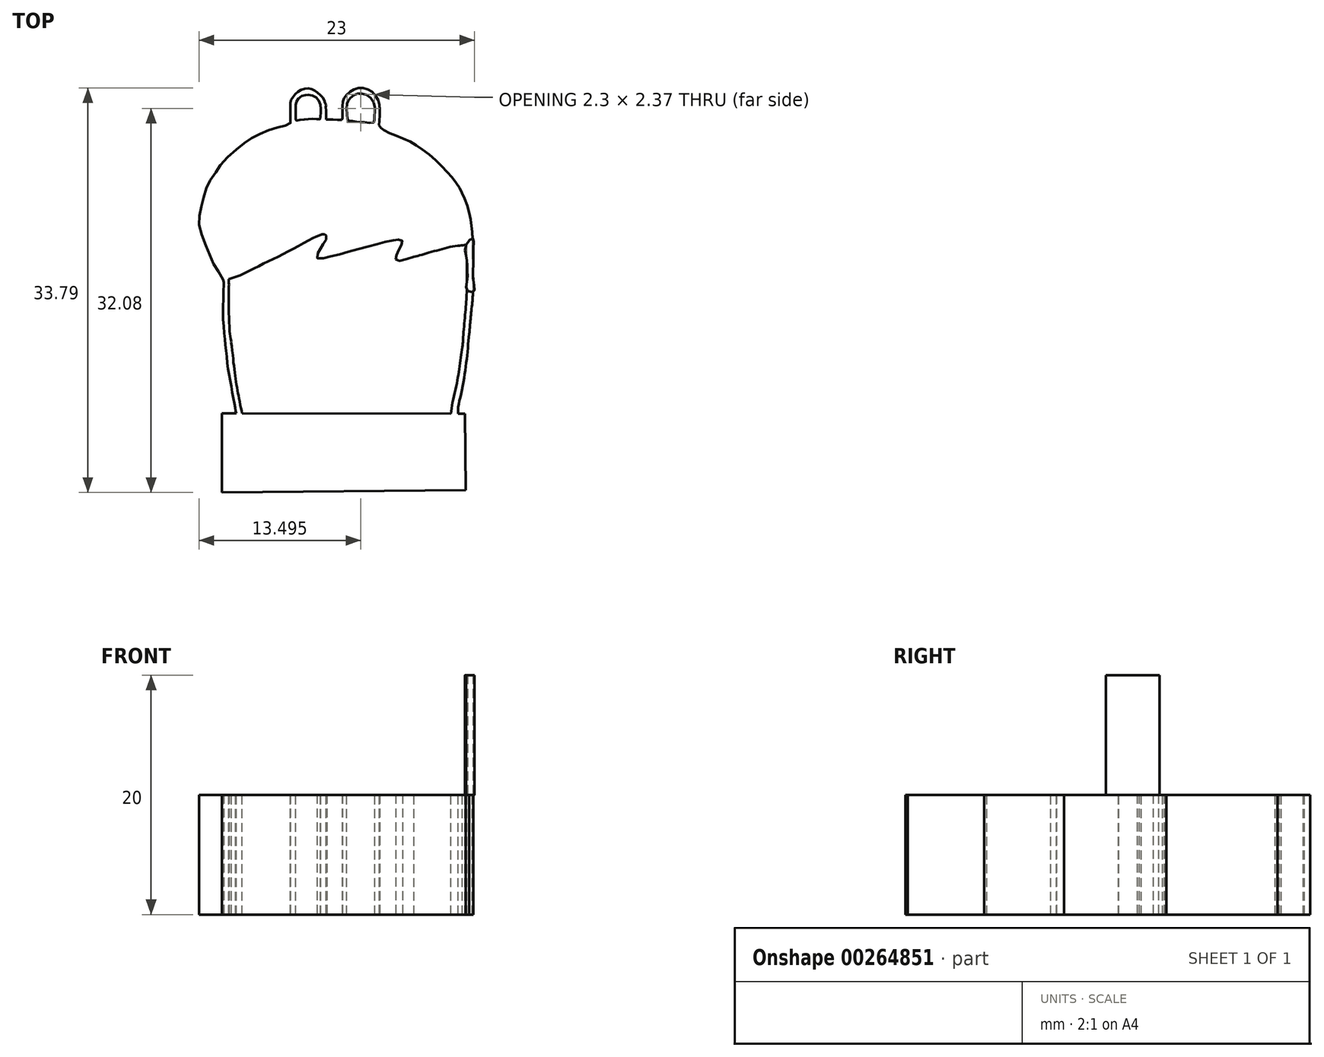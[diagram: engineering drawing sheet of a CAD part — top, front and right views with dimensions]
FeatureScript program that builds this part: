
annotation { "Feature Type Name" : "Feature", "Feature Type Description" : "" }
export const myFeature = defineFeature(function(context is Context, id is Id, definition is map)
    precondition{}
    {
        {
            var Q0;
            Q0=qCreatedBy(makeId("Top.planeOp"),FACE);
            var sketch = newSketch(context, id + "F0", { "sketchPlane" : qUnion([Q0])});
            skFitSpline(sketch, "E0", {"points": [v(-8.8, 2.1) * mm, v(-8.4, 2.24) * mm, v(-7.67, 2.52) * mm, v(-6.78, 2.96) * mm, v(-5.81, 3.45) * mm, v(-4.83, 3.93) * mm, v(-3.79, 4.44) * mm, v(-2.68, 5.05) * mm, v(-1.76, 5.56) * mm, v(-1.35, 5.71) * mm, v(-1.03, 5.86) * mm, v(-0.82, 5.85) * mm, v(-0.68, 5.76) * mm], "startDerivative": vector(5.65, 1.9) * mm, "endDerivative": vector(3.17, -2.45) * mm});
            skFitSpline(sketch, "E1", {"points": [v(-0.68, 5.76) * mm, v(-0.61, 5.57) * mm, v(-0.78, 5.3) * mm, v(-0.97, 5) * mm, v(-1.11, 4.72) * mm, v(-1.3, 4.4) * mm, v(-1.42, 4.12) * mm, v(-1.41, 3.83) * mm, v(-1.02, 3.82) * mm, v(-0.43, 3.99) * mm, v(0.48, 4.17) * mm, v(1.43, 4.47) * mm, v(2.69, 4.8) * mm, v(3.65, 5.05) * mm, v(4.39, 5.26) * mm, v(5.07, 5.36) * mm, v(5.34, 5.41) * mm, v(5.58, 5.38) * mm, v(5.7, 5.27) * mm, v(5.62, 5.03) * mm, v(5.5, 4.75) * mm, v(5.3, 4.37) * mm, v(5.18, 4.08) * mm, v(5.12, 3.85) * mm, v(5.18, 3.65) * mm, v(5.42, 3.64) * mm, v(6.02, 3.76) * mm, v(6.65, 3.96) * mm], "startDerivative": vector(4.5, -7.51) * mm, "endDerivative": vector(13.56, 4.53) * mm});
            skFitSpline(sketch, "E2", {"points": [v(6.65, 3.96) * mm, v(7.15, 4.1) * mm, v(7.84, 4.32) * mm, v(8.74, 4.54) * mm, v(9.73, 4.81) * mm, v(10.44, 4.9) * mm, v(10.8, 4.95) * mm, v(11, 4.95) * mm, v(11.03, 4.8) * mm, v(11.04, 4) * mm, v(11.05, 3.1) * mm, v(11.06, 2.1) * mm, v(11.05, 1.1) * mm, v(10.99, 0) * mm, v(10.86, -1.43) * mm, v(10.74, -2.88) * mm, v(10.69, -3.57) * mm], "startDerivative": vector(9.32, 2.38) * mm, "endDerivative": vector(-1.16, -10.46) * mm});
            skFitSpline(sketch, "E3", {"points": [v(11.26, -2.47) * mm, v(11.32, -1.74) * mm, v(11.43, -0.57) * mm, v(11.54, 0.6) * mm, v(11.58, 1.5) * mm, v(11.56, 2.8) * mm, v(11.55, 3.79) * mm, v(11.52, 4.76) * mm, v(11.52, 5.42) * mm, v(11.49, 6.07) * mm], "startDerivative": vector(0.56, 7) * mm, "endDerivative": vector(-0.91, 7.3) * mm});
            skFitSpline(sketch, "E4", {"points": [v(11.49, 6.07) * mm, v(11.41, 6.74) * mm, v(11.26, 7.62) * mm, v(10.96, 8.63) * mm, v(10.63, 9.37) * mm, v(10.37, 9.84) * mm, v(9.84, 10.58) * mm, v(9.17, 11.33) * mm, v(8.18, 12.3) * mm, v(7.1, 13.1) * mm, v(6.27, 13.6) * mm, v(5.2, 14.08) * mm, v(4.42, 14.38) * mm, v(3.93, 14.71) * mm, v(3.83, 14.79) * mm, v(3.73, 14.97) * mm, v(3.75, 15.34) * mm], "startDerivative": vector(-1.2, 10.67) * mm, "endDerivative": vector(-0.34, 9.32) * mm});
            skFitSpline(sketch, "E5", {"points": [v(3.75, 15.34) * mm, v(3.78, 16.03) * mm, v(3.75, 16.66) * mm, v(3.63, 17.11) * mm, v(3.24, 17.64) * mm, v(2.83, 17.94) * mm, v(2.27, 18.07) * mm, v(1.8, 18.01) * mm, v(1.35, 17.8) * mm, v(1, 17.5) * mm, v(0.78, 17.16) * mm, v(0.7, 16.86) * mm, v(0.66, 16.36) * mm, v(0.66, 16.03) * mm, v(0.66, 15.73) * mm, v(0.65, 15.47) * mm, v(0.62, 15.42) * mm, v(0.33, 15.41) * mm, v(-0.19, 15.43) * mm, v(-0.5, 15.43) * mm, v(-0.7, 15.43) * mm], "startDerivative": vector(0.4, 10.64) * mm, "endDerivative": vector(-5.55, -0.03) * mm});
            skCircle(sketch, "E6", {"center": v(6.09, -0.5) * mm, "radius": 3.15 * mm});
            skPoint(sketch, "E6.first.point", {"position": v(5.98, 2.65) * mm});
            skPoint(sketch, "E6.second.point", {"position": v(6.02, -3.65) * mm});
            skPoint(sketch, "E6.third.point", {"position": v(9.22, -0.2) * mm});
            skCircle(sketch, "E7", {"center": v(6.08, -0.54) * mm, "radius": 2.63 * mm});
            skPoint(sketch, "E7.first.point", {"position": v(5.98, 2.1) * mm});
            skPoint(sketch, "E7.second.point", {"position": v(5.98, -3.17) * mm});
            skPoint(sketch, "E7.third.point", {"position": v(8.7, -0.58) * mm});
            skCircle(sketch, "E8", {"center": v(7.16, -0.53) * mm, "radius": 1.28 * mm});
            skPoint(sketch, "E8.first.point", {"position": v(7.12, 0.75) * mm});
            skPoint(sketch, "E8.second.point", {"position": v(7.22, -1.8) * mm});
            skPoint(sketch, "E8.third.point", {"position": v(8.43, -0.49) * mm});
            skCircle(sketch, "E9", {"center": v(-4.02, -0.63) * mm, "radius": 3.11 * mm});
            skPoint(sketch, "E9.first.point", {"position": v(-4.2, 2.47) * mm});
            skPoint(sketch, "E9.second.point", {"position": v(-3.86, -3.74) * mm});
            skPoint(sketch, "E9.third.point", {"position": v(-1.05, 0.3) * mm});
            skCircle(sketch, "E10", {"center": v(-4.04, -0.66) * mm, "radius": 2.65 * mm});
            skPoint(sketch, "E10.first.point", {"position": v(-4.2, 1.99) * mm});
            skPoint(sketch, "E10.second.point", {"position": v(-3.9, -3.3) * mm});
            skPoint(sketch, "E10.third.point", {"position": v(-1.39, -0.71) * mm});
            skCircle(sketch, "E11", {"center": v(-2.97, -0.61) * mm, "radius": 1.26 * mm});
            skPoint(sketch, "E11.first.point", {"position": v(-2.97, 0.64) * mm});
            skPoint(sketch, "E11.second.point", {"position": v(-2.96, -1.87) * mm});
            skPoint(sketch, "E11.third.point", {"position": v(-1.72, -0.58) * mm});
            skFitSpline(sketch, "E12", {"points": [v(0.31, -3.75) * mm, v(0.56, -3.78) * mm, v(0.87, -3.93) * mm, v(0.95, -3.99) * mm, v(1.05, -3.93) * mm, v(1.33, -3.75) * mm, v(1.71, -3.7) * mm, v(2, -3.87) * mm, v(2.13, -4.19) * mm, v(2.02, -4.46) * mm, v(1.77, -4.62) * mm, v(1.4, -4.73) * mm, v(1, -4.78) * mm, v(0.6, -4.75) * mm, v(0.25, -4.68) * mm, v(0, -4.54) * mm, v(-0.17, -4.24) * mm, v(-0.13, -3.95) * mm, v(0.05, -3.79) * mm, v(0.31, -3.75) * mm]});
            skFitSpline(sketch, "E13", {"points": [v(-3.23, 15.5) * mm, v(-3.24, 16.06) * mm, v(-3.24, 16.53) * mm, v(-3.2, 16.85) * mm, v(-3.06, 17.13) * mm, v(-2.75, 17.38) * mm, v(-2.45, 17.48) * mm, v(-2.2, 17.5) * mm, v(-1.77, 17.42) * mm, v(-1.43, 17.19) * mm, v(-1.2, 16.82) * mm, v(-1.16, 16.43) * mm, v(-1.15, 16.01) * mm, v(-1.16, 15.67) * mm, v(-1.18, 15.48) * mm, v(-1.42, 15.47) * mm, v(-1.84, 15.49) * mm, v(-2.2, 15.48) * mm, v(-2.65, 15.42) * mm, v(-3.07, 15.37) * mm, v(-3.22, 15.35) * mm, v(-3.23, 15.5) * mm]});
            skFitSpline(sketch, "E14", {"points": [v(1.07, 15.46) * mm, v(1.04, 15.89) * mm, v(1.04, 16.39) * mm, v(1.06, 16.83) * mm, v(1.12, 16.97) * mm, v(1.2, 17.1) * mm, v(1.43, 17.33) * mm, v(1.7, 17.5) * mm, v(1.96, 17.59) * mm, v(2.28, 17.6) * mm, v(2.68, 17.5) * mm, v(3.04, 17.22) * mm, v(3.3, 16.78) * mm, v(3.37, 16.4) * mm, v(3.36, 16.07) * mm, v(3.35, 15.74) * mm, v(3.34, 15.45) * mm, v(3.32, 15.22) * mm, v(3.26, 15.18) * mm, v(3, 15.16) * mm, v(2.56, 15.2) * mm, v(2.2, 15.23) * mm, v(1.9, 15.25) * mm, v(1.63, 15.28) * mm, v(1.37, 15.31) * mm, v(1.16, 15.33) * mm, v(1.1, 15.37) * mm, v(1.07, 15.46) * mm]});
            skLineSegment(sketch, "E15", {"start": v(-9.39, -9.12) * mm, "end": v(-9.39, -15.72) * mm});
            skLineSegment(sketch, "E16", {"start": v(-9.39, -15.72) * mm, "end": v(10.95, -15.53) * mm});
            skLineSegment(sketch, "E17", {"start": v(10.95, -15.53) * mm, "end": v(10.89, -9.14) * mm});
            skFitSpline(sketch, "E18", {"points": [v(-0.7, 15.43) * mm, v(-0.7, 16.1) * mm, v(-0.7, 16.56) * mm, v(-0.7, 16.65) * mm, v(-0.77, 16.82) * mm, v(-0.88, 17.1) * mm, v(-1.04, 17.33) * mm, v(-1.35, 17.64) * mm, v(-1.71, 17.88) * mm, v(-2.07, 18.03) * mm, v(-2.5, 18) * mm, v(-2.92, 17.83) * mm, v(-3.26, 17.56) * mm, v(-3.54, 17.2) * mm, v(-3.67, 16.9) * mm, v(-3.7, 16.38) * mm, v(-3.69, 16.04) * mm, v(-3.68, 15.66) * mm], "startDerivative": vector(0.03, 8.48) * mm, "endDerivative": vector(0.2, -6.68) * mm});
            skFitSpline(sketch, "E19", {"points": [v(-3.68, 15.66) * mm, v(-3.68, 15.28) * mm, v(-3.68, 15.13) * mm, v(-3.68, 15.1) * mm, v(-3.9, 15) * mm, v(-4.43, 14.84) * mm, v(-4.92, 14.72) * mm, v(-5.58, 14.51) * mm, v(-6.18, 14.25) * mm, v(-6.79, 13.95) * mm, v(-7.26, 13.68) * mm, v(-7.78, 13.27) * mm, v(-8.45, 12.7) * mm, v(-9.15, 12.05) * mm, v(-9.63, 11.47) * mm, v(-9.92, 11) * mm, v(-10.32, 10.44) * mm, v(-10.61, 9.87) * mm, v(-10.8, 9.34) * mm, v(-10.97, 8.67) * mm, v(-11.15, 8.03) * mm, v(-11.26, 7.36) * mm, v(-11.3, 6.75) * mm, v(-11.15, 6.09) * mm, v(-10.84, 5.13) * mm, v(-10.51, 4.42) * mm, v(-10.25, 3.68) * mm, v(-9.95, 3.17) * mm, v(-9.6, 2.63) * mm, v(-9.29, 2.08) * mm], "startDerivative": vector(0.15, -14.8) * mm, "endDerivative": vector(7.87, -15.58) * mm});
            skFitSpline(sketch, "E20", {"points": [v(-9.29, 2.08) * mm, v(-9.24, 1.84) * mm, v(-9.24, 1.67) * mm, v(-9.29, 0.19) * mm, v(-9.29, -1.17) * mm, v(-9.18, -2.54) * mm, v(-9.08, -3.52) * mm, v(-8.96, -4.65) * mm, v(-8.83, -5.7) * mm, v(-8.63, -6.74) * mm, v(-8.44, -7.8) * mm, v(-8.3, -8.55) * mm, v(-8.25, -8.93) * mm], "startDerivative": vector(1.42, -6.07) * mm, "endDerivative": vector(0.55, -6.27) * mm});
            skPoint(sketch, "E21", {"position": v(-7.7, -9.12) * mm});
            skPoint(sketch, "E22", {"position": v(-8.2, -9.12) * mm});
            skFitSpline(sketch, "E23", {"points": [v(-8.25, -8.93) * mm, v(-8.2, -9.12) * mm], "startDerivative": vector(0.05, -0.2) * mm, "endDerivative": vector(0.05, -0.2) * mm});
            skFitSpline(sketch, "E24", {"points": [v(-7.7, -9.12) * mm, v(-7.84, -8.5) * mm, v(-7.99, -7.74) * mm, v(-8.08, -7.23) * mm, v(-8.21, -6.57) * mm, v(-8.3, -5.92) * mm, v(-8.4, -5.08) * mm, v(-8.51, -4.03) * mm, v(-8.62, -3.09) * mm, v(-8.6, -3.09) * mm], "startDerivative": vector(-1.1, 5.28) * mm, "endDerivative": vector(0.63, -0.3) * mm});
            skFitSpline(sketch, "E25", {"points": [v(-8.6, -3.09) * mm, v(-8.72, -2.5) * mm, v(-8.77, -1.86) * mm, v(-8.8, -1) * mm, v(-8.81, 0) * mm, v(-8.83, 1.11) * mm, v(-8.8, 1.47) * mm, v(-8.8, 1.75) * mm, v(-8.8, 2.1) * mm], "startDerivative": vector(-1.04, 4.82) * mm, "endDerivative": vector(0.02, 3.77) * mm});
            skLineSegment(sketch, "E26", {"start": v(-8.2, -9.12) * mm, "end": v(-9.39, -9.12) * mm});
            skLineSegment(sketch, "E27", {"start": v(-7.7, -9.12) * mm, "end": v(9.72, -9.14) * mm});
            skLineSegment(sketch, "E28", {"start": v(10.89, -9.14) * mm, "end": v(10.34, -9.14) * mm});
            skFitSpline(sketch, "E29", {"points": [v(10.69, -3.57) * mm, v(10.53, -4.5) * mm, v(10.39, -5.58) * mm, v(10.2, -6.68) * mm, v(9.88, -8.08) * mm, v(9.72, -9.14) * mm], "startDerivative": vector(-0.8, -4.96) * mm, "endDerivative": vector(-0.61, -5.17) * mm});
            skFitSpline(sketch, "E30", {"points": [v(11.26, -2.47) * mm, v(11.15, -3.45) * mm, v(11.04, -4.57) * mm, v(10.9, -5.72) * mm, v(10.69, -7) * mm, v(10.42, -8.1) * mm, v(10.32, -8.78) * mm, v(10.34, -9.14) * mm], "startDerivative": vector(-0.71, -6.55) * mm, "endDerivative": vector(0.44, -3.74) * mm});
            skLineSegment(sketch, "E31", {"start": v(10.34, -9.14) * mm, "end": v(9.72, -9.14) * mm});
            skSolve(sketch);
        }
        {
            var Q0;
            Q0=makeQuery(id+"F0.imprint","IMPRINT",FACE,{"disambiguationData":[TD([[makeQuery(id+"F0.imprint","IMPRINT",EDGE,{"derivedFrom":sQuery(id+"F0.wireOp",EDGE,"E0")}),1.0]])]});
            extrude(context, id + "F1", {"entities" : qUnion([Q0]), "oppositeDirection" : true, "depth" : 10 * mm});
        }
        {
            var Q0;
            Q0=qCreatedBy(makeId("Top.planeOp"),FACE);
            cPlane(context, id + "F2", {"entities" : qUnion([Q0]), "cplaneType" : CPlaneType.OFFSET, "offset" : 0 * mm, "width" : 150 * mm, "height" : 150 * mm});
        }
        {
            var Q0;
            Q0=qCreatedBy(id+"F2.planeOp",FACE);
            var sketch = newSketch(context, id + "F3", { "sketchPlane" : qUnion([Q0])});
            skFitSpline(sketch, "E32", {"points": [v(10.98, 4.97) * mm, v(11, 3.98) * mm, v(11.08, 3.09) * mm, v(11.08, 2.02) * mm, v(11.04, 1.2) * mm, v(11.63, 1.06) * mm, v(11.63, 1.71) * mm, v(11.56, 2.67) * mm, v(11.6, 3.5) * mm, v(11.6, 4.7) * mm, v(11.56, 5.49) * mm, v(10.98, 4.97) * mm]});
            skSolve(sketch);
        }
        {
            var Q0;
            Q0=makeQuery(id+"F3.imprint","IMPRINT",FACE,{"disambiguationData":[TD([[makeQuery(id+"F3.imprint","IMPRINT",EDGE,{"derivedFrom":sQuery(id+"F3.wireOp",EDGE,"E32")}),1.0]])]});
            extrude(context, id + "F4", {"entities" : qUnion([Q0]), "operationType" : NewBodyOperationType.ADD, "depth" : 10 * mm});
        }
    });
